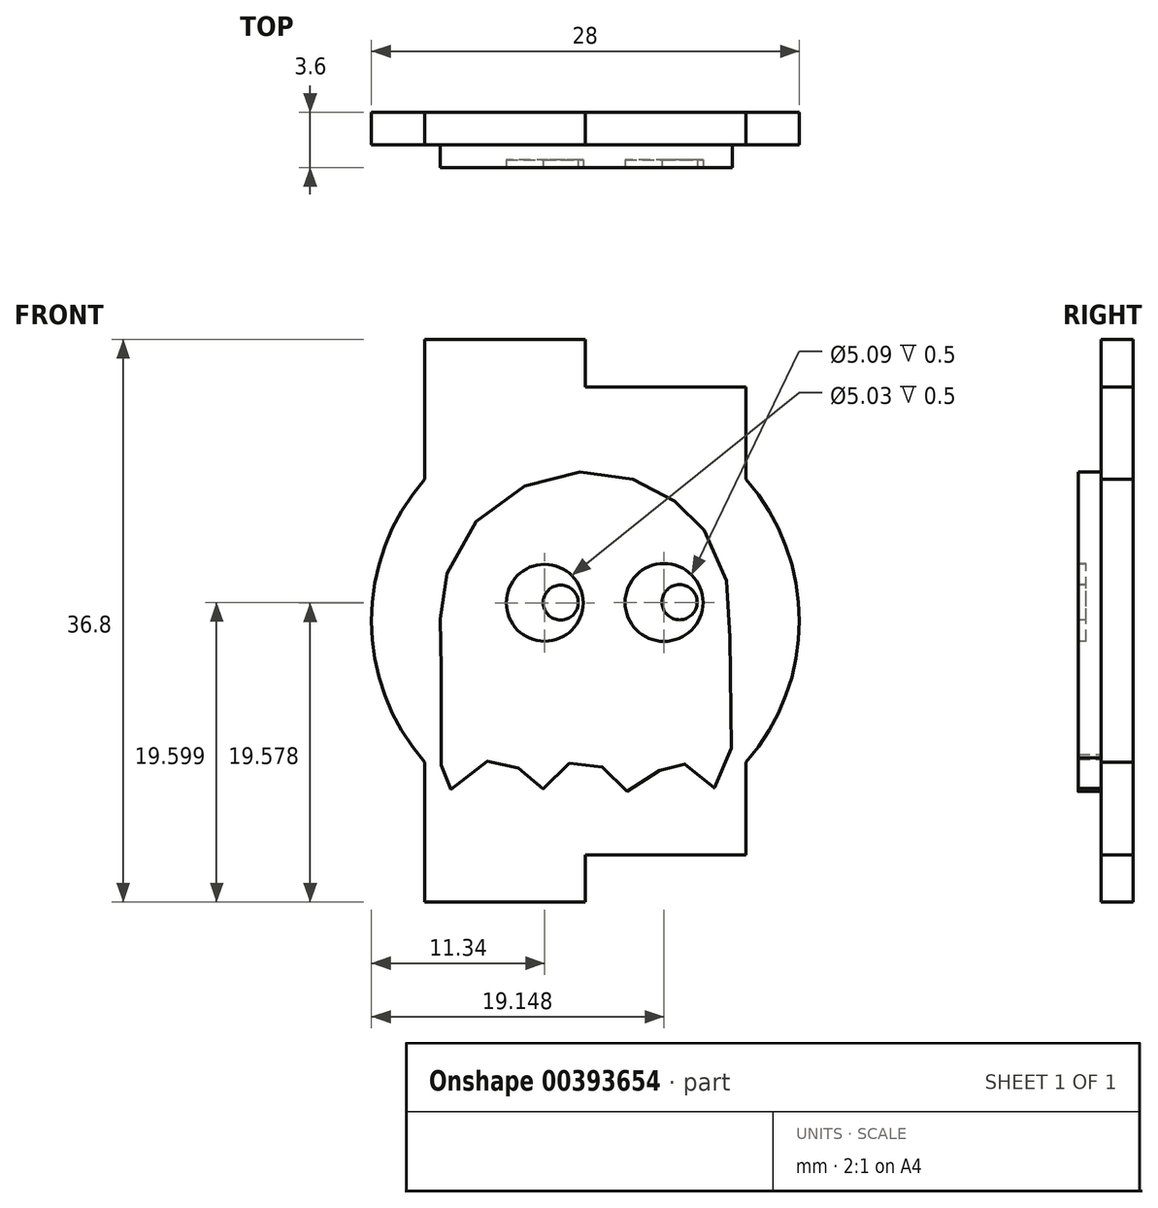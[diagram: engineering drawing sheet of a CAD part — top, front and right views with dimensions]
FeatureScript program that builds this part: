
annotation { "Feature Type Name" : "Feature", "Feature Type Description" : "" }
export const myFeature = defineFeature(function(context is Context, id is Id, definition is map)
    precondition{}
    {
        {
            var Q0;
            Q0=qCreatedBy(makeId("Front.planeOp"),FACE);
            var sketch = newSketch(context, id + "F0", { "sketchPlane" : qUnion([Q0])});
            skArc(sketch, "E0", {"start": v(-10.5, 9.26) * mm, "mid": v(-14, 0) * mm, "end": v(-10.5, -9.26) * mm});
            skLineSegment(sketch, "E1", {"start": v(0, 18.4) * mm, "end": v(-10.5, 18.4) * mm});
            skLineSegment(sketch, "E2", {"start": v(0, 18.4) * mm, "end": v(0, 15.3) * mm});
            skLineSegment(sketch, "E3", {"start": v(0, 15.3) * mm, "end": v(10.5, 15.3) * mm});
            skLineSegment(sketch, "E4", {"start": v(10.5, 15.3) * mm, "end": v(10.5, 9.26) * mm});
            skLineSegment(sketch, "E5", {"start": v(-10.5, 18.4) * mm, "end": v(-10.5, 9.26) * mm});
            skLineSegment(sketch, "E6", {"start": v(0, -18.4) * mm, "end": v(-10.5, -18.4) * mm});
            skLineSegment(sketch, "E7", {"start": v(0, -18.4) * mm, "end": v(0, -15.3) * mm});
            skLineSegment(sketch, "E8", {"start": v(0, -15.3) * mm, "end": v(10.5, -15.3) * mm});
            skLineSegment(sketch, "E9", {"start": v(10.5, -15.3) * mm, "end": v(10.5, -9.26) * mm});
            skLineSegment(sketch, "E10", {"start": v(-10.5, -18.4) * mm, "end": v(-10.5, -9.26) * mm});
            skArc(sketch, "E11.trimOffspring", {"start": v(10.5, -9.26) * mm, "mid": v(14, 0) * mm, "end": v(10.5, 9.26) * mm});
            skSolve(sketch);
        }
        {
            var Q0;
            Q0=makeQuery(id+"F0.imprint","IMPRINT",FACE,{"disambiguationData":[TD([[makeQuery(id+"F0.imprint","IMPRINT",EDGE,{"derivedFrom":sQuery(id+"F0.wireOp",EDGE,"E0")}),1.0]])]});
            extrude(context, id + "F1", {"entities" : qUnion([Q0]), "depth" : 2.1 * mm, "offsetDistance" : 25 * mm});
        }
        {
            var Q0;
            Q0=makeQuery(id+"F1.opExtrude","CAP_FACE",FACE,{"disambiguationData":[OSD([sQuery(id+"F0.wireOp",EDGE,"E0"),sQuery(id+"F0.wireOp",EDGE,"E1"),sQuery(id+"F0.wireOp",EDGE,"E2"),sQuery(id+"F0.wireOp",EDGE,"E3"),sQuery(id+"F0.wireOp",EDGE,"E4"),sQuery(id+"F0.wireOp",EDGE,"E5"),sQuery(id+"F0.wireOp",EDGE,"E6"),sQuery(id+"F0.wireOp",EDGE,"E7"),sQuery(id+"F0.wireOp",EDGE,"E8"),sQuery(id+"F0.wireOp",EDGE,"E9"),sQuery(id+"F0.wireOp",EDGE,"E10"),sQuery(id+"F0.wireOp",EDGE,"E11.trimOffspring")])],"isStart":false});
            var sketch = newSketch(context, id + "F2", { "sketchPlane" : qUnion([Q0])});
            skFitSpline(sketch, "E12", {"points": [v(-3.97, 8.83) * mm, v(-7.6, 5.97) * mm, v(-9.32, 2.03) * mm, v(-9.5, 0) * mm, v(-9.46, -0.54) * mm, v(-9.42, -9.83) * mm, v(-9.35, -10.11) * mm, v(-8.8, -11.03) * mm, v(-6.68, -9.4) * mm, v(-5.13, -8.84) * mm, v(-3.72, -10.6) * mm, v(-2.88, -11.03) * mm, v(-1.26, -9.76) * mm, v(-0.84, -9.13) * mm, v(1, -9.48) * mm, v(2.12, -10.81) * mm, v(3.32, -11.1) * mm, v(5, -9.62) * mm, v(5.92, -8.98) * mm, v(7.26, -10.18) * mm, v(8.53, -10.96) * mm, v(9.37, -9.9) * mm, v(9.3, 1.79) * mm, v(9.16, 2.84) * mm, v(7.26, 6.71) * mm, v(5.92, 7.77) * mm, v(3.53, 9.1) * mm, v(0, 9.74) * mm, v(-3.97, 8.83) * mm]});
            skSolve(sketch);
        }
        {
            var Q0;
            Q0=makeQuery(id+"F2.imprint","IMPRINT",FACE,{"disambiguationData":[TD([[makeQuery(id+"F2.imprint","IMPRINT",EDGE,{"derivedFrom":sQuery(id+"F2.wireOp",EDGE,"E12")}),1.0]])]});
            extrude(context, id + "F3", {"entities" : qUnion([Q0]), "operationType" : NewBodyOperationType.ADD, "depth" : 1.5 * mm, "offsetDistance" : 25 * mm});
        }
        {
            var Q0;
            Q0=makeQuery(id+"F3.opExtrude","CAP_FACE",FACE,{"disambiguationData":[OSD([sQuery(id+"F2.wireOp",EDGE,"E12")])],"isStart":false});
            var sketch = newSketch(context, id + "F4", { "sketchPlane" : qUnion([Q0])});
            skCircle(sketch, "E13", {"center": v(-2.66, 1.18) * mm, "radius": 2.52 * mm});
            skPoint(sketch, "E13.first.point", {"position": v(-3.65, 3.5) * mm});
            skPoint(sketch, "E13.second.point", {"position": v(-1.52, -1.06) * mm});
            skPoint(sketch, "E13.third.point", {"position": v(-4.88, 0) * mm});
            skCircle(sketch, "E14", {"center": v(-1.61, 1.2) * mm, "radius": 1.14 * mm});
            skPoint(sketch, "E14.first.point", {"position": v(-2.13, 2.21) * mm});
            skPoint(sketch, "E14.second.point", {"position": v(-1.08, 0.18) * mm});
            skPoint(sketch, "E14.third.point", {"position": v(-0.47, 1.26) * mm});
            skCircle(sketch, "E15", {"center": v(6.16, 1.22) * mm, "radius": 1.15 * mm});
            skPoint(sketch, "E15.first.point", {"position": v(5.24, 1.9) * mm});
            skPoint(sketch, "E15.second.point", {"position": v(6.57, 2.3) * mm});
            skPoint(sketch, "E15.third.point", {"position": v(6.97, 0.4) * mm});
            skCircle(sketch, "E16", {"center": v(5.15, 1.2) * mm, "radius": 2.55 * mm});
            skPoint(sketch, "E16.first.point", {"position": v(3.25, 2.9) * mm});
            skPoint(sketch, "E16.second.point", {"position": v(5.93, -1.23) * mm});
            skPoint(sketch, "E16.third.point", {"position": v(7.54, 2.09) * mm});
            skSolve(sketch);
        }
        {
            var Q0;
            Q0=makeQuery(id+"F4.imprint","IMPRINT",FACE,{"disambiguationData":[TD([[makeQuery(id+"F4.imprint","IMPRINT",EDGE,{"derivedFrom":sQuery(id+"F4.wireOp",EDGE,"E13")}),1.0]])]});
            var Q1;
            Q1=makeQuery(id+"F4.imprint","IMPRINT",FACE,{"disambiguationData":[TD([[makeQuery(id+"F4.imprint","IMPRINT",EDGE,{"derivedFrom":sQuery(id+"F4.wireOp",EDGE,"E15")}),-1.0]])]});
            extrude(context, id + "F5", {"entities" : qUnion([Q0, Q1]), "operationType" : NewBodyOperationType.REMOVE, "oppositeDirection" : true, "depth" : 0.5 * mm});
        }
    });
